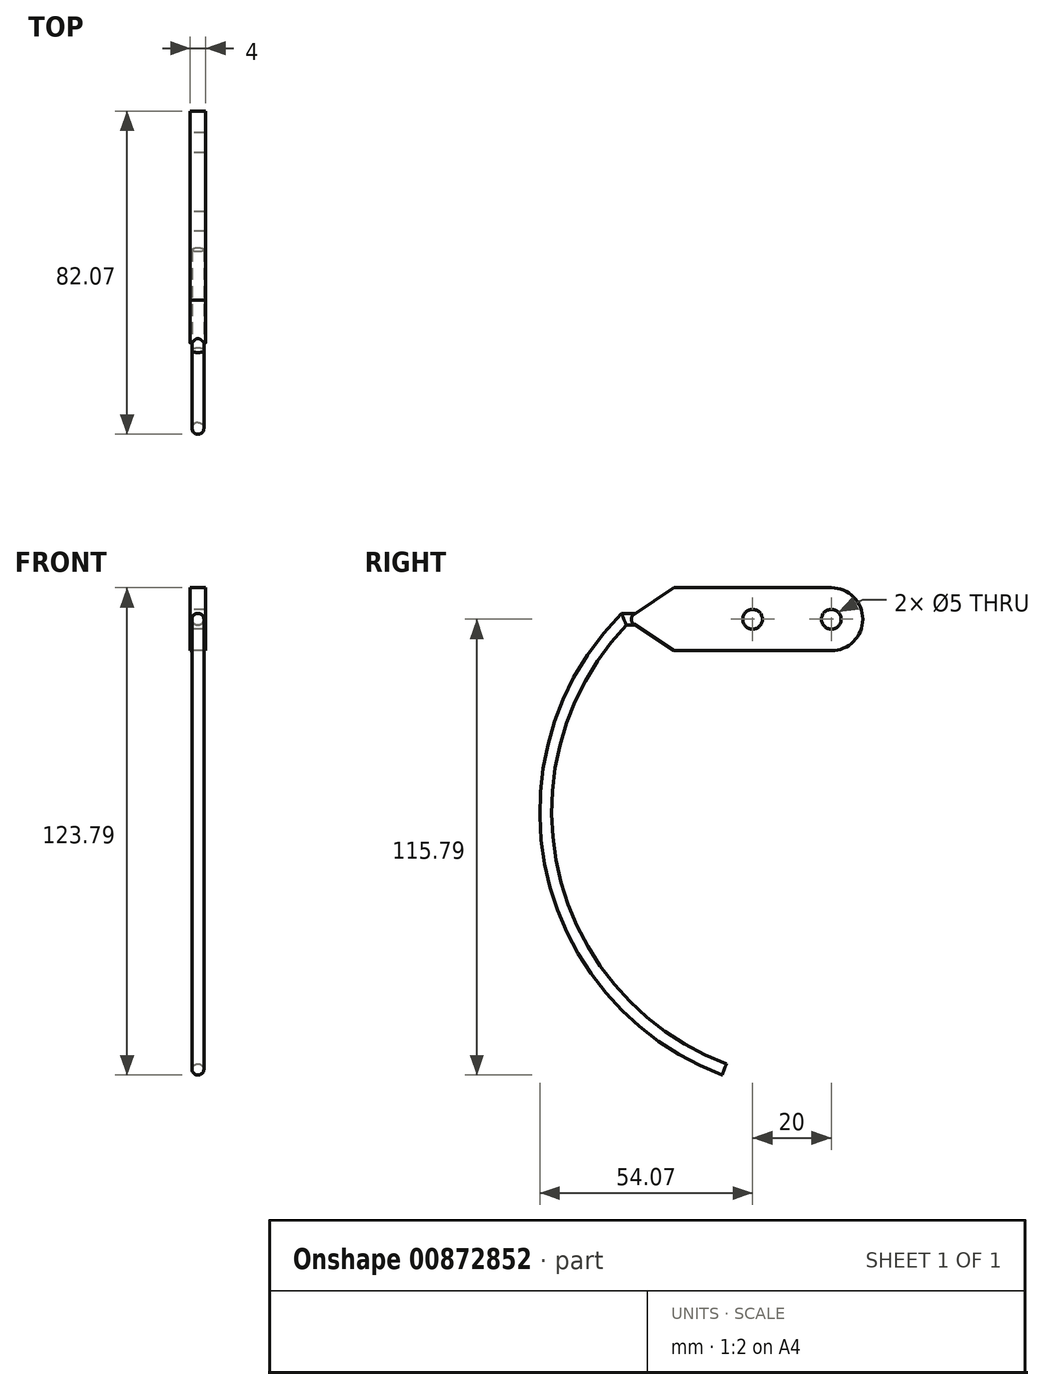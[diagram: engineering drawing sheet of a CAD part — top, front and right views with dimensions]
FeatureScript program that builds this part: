
annotation { "Feature Type Name" : "Feature", "Feature Type Description" : "" }
export const myFeature = defineFeature(function(context is Context, id is Id, definition is map)
    precondition{}
    {
        {
            var Q0;
            Q0=qCreatedBy(makeId("Right.planeOp"),FACE);
            var sketch = newSketch(context, id + "F0", { "sketchPlane" : qUnion([Q0])});
            skArc(sketch, "E0", {"start": v(0, -8) * mm, "mid": v(8, 0) * mm, "end": v(0, 8) * mm});
            skLineSegment(sketch, "E1", {"start": v(-40, 8) * mm, "end": v(0, 8) * mm});
            skLineSegment(sketch, "E2", {"start": v(0, -8) * mm, "end": v(-40, -8) * mm});
            skCircle(sketch, "E3", {"center": v(0, 0) * mm, "radius": 2.5 * mm});
            skCircle(sketch, "E4", {"center": v(-20, 0) * mm, "radius": 2.5 * mm});
            skLineSegment(sketch, "E5", {"start": v(-40, 8) * mm, "end": v(-40, -8) * mm});
            skSolve(sketch);
        }
        {
            var Q0;
            Q0 = qSketchRegion(id + "F0", true);
            extrude(context, id + "F1", {"entities" : qUnion([Q0]), "endBound" : BoundingType.SYMMETRIC, "depth" : 4 * mm, "offsetDistance" : 25 * mm});
        }
        {
            var Q0;
            Q0=qCreatedBy(makeId("Right.planeOp"),FACE);
            var sketch = newSketch(context, id + "F2", { "sketchPlane" : qUnion([Q0])});
            skArc(sketch, "E6", {"start": v(-52.7, 0) * mm, "mid": v(-70.9, -64.1) * mm, "end": v(-27.2, -114.39) * mm});
            skLineSegment(sketch, "E7", {"start": v(-52.7, 0) * mm, "end": v(-37.74, 0) * mm});
            skSolve(sketch);
        }
        {
            var Q0;
            Q0=makeQuery(id+"F1.opExtrude","SWEPT_FACE",FACE,{"disambiguationData":[OSD([sQuery(id+"F0.wireOp",EDGE,"E5")])]});
            var sketch = newSketch(context, id + "F3", { "sketchPlane" : qUnion([Q0])});
            skCircle(sketch, "E8", {"center": v(0, 0) * mm, "radius": 1.5 * mm});
            skSolve(sketch);
        }
        {
            var Q0;
            Q0=makeQuery(id+"F3.imprint","IMPRINT",FACE,{"disambiguationData":[TD([[makeQuery(id+"F3.imprint","IMPRINT",EDGE,{"derivedFrom":sQuery(id+"F3.wireOp",EDGE,"E8")}),1.0]])]});
            var Q1;
            Q1=sQuery(id+"F2.wireOp",EDGE,"E6");
            var Q2;
            Q2=sQuery(id+"F2.wireOp",EDGE,"E7");
            sweep(context, id + "F4", {"operationType" : NewBodyOperationType.ADD, "profiles" : qUnion([Q0]), "path" : qUnion([Q1, Q2])});
        }
        {
            var Q0;
            Q0=qCreatedBy(makeId("Right.planeOp"),FACE);
            var sketch = newSketch(context, id + "F5", { "sketchPlane" : qUnion([Q0])});
            skLineSegment(sketch, "E9", {"start": v(-40, 8) * mm, "end": v(-50.13, 1.25) * mm});
            skLineSegment(sketch, "E10", {"start": v(-50.13, -1.25) * mm, "end": v(-40, -8) * mm});
            skLineSegment(sketch, "E11", {"start": v(-40, -8) * mm, "end": v(-40, 8) * mm});
            skArc(sketch, "E12", {"start": v(-50.13, 1.25) * mm, "mid": v(-50.8, 0) * mm, "end": v(-50.13, -1.25) * mm});
            skPoint(sketch, "E13.orphan", {"position": v(-52, 0) * mm});
            skSolve(sketch);
        }
        {
            var Q0;
            Q0=makeQuery(id+"F5.imprint","IMPRINT",FACE,{"disambiguationData":[TD([[makeQuery(id+"F5.imprint","IMPRINT",EDGE,{"derivedFrom":sQuery(id+"F5.wireOp",EDGE,"E9")}),1.0]])]});
            extrude(context, id + "F6", {"entities" : qUnion([Q0]), "operationType" : NewBodyOperationType.ADD, "endBound" : BoundingType.SYMMETRIC, "depth" : 4 * mm, "offsetDistance" : 25 * mm});
        }
    });
